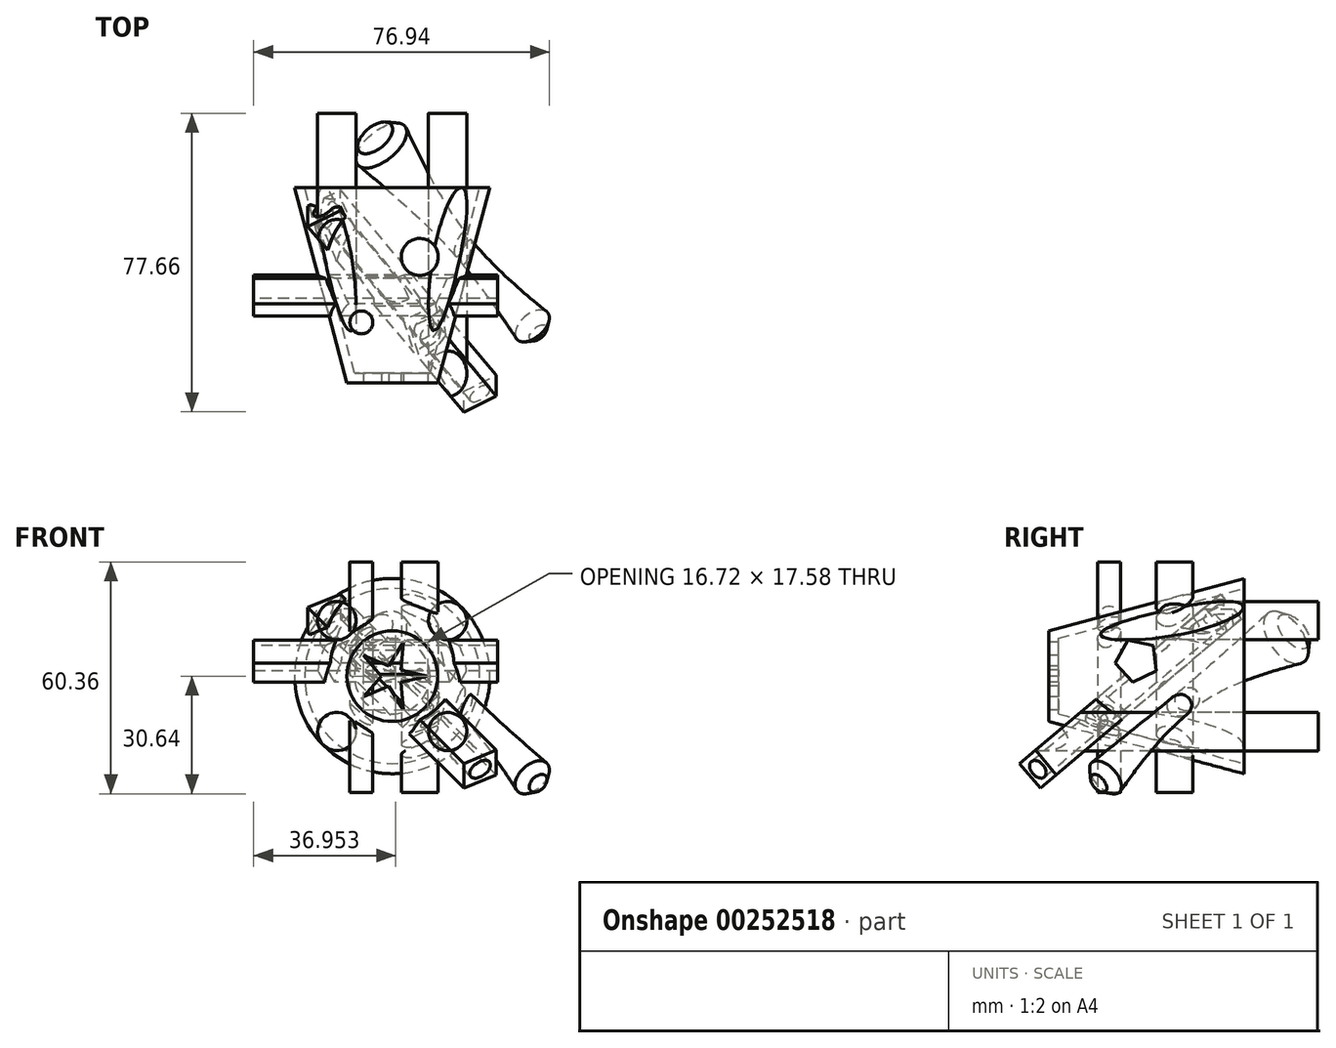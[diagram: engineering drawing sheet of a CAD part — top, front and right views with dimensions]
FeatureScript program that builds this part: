
annotation { "Feature Type Name" : "Feature", "Feature Type Description" : "" }
export const myFeature = defineFeature(function(context is Context, id is Id, definition is map)
    precondition{}
    {
        {
            var Q0;
            Q0=qCreatedBy(makeId("Front.planeOp"),FACE);
            var sketch = newSketch(context, id + "F0", { "sketchPlane" : qUnion([Q0])});
            skCircle(sketch, "E0", {"center": v(0, 0) * mm, "radius": 25.4 * mm});
            skSolve(sketch);
        }
        {
            var Q0;
            Q0 = qSketchRegion(id + "F0", true);
            extrude(context, id + "F1", {"entities" : qUnion([Q0]), "depth" : 50.8 * mm, "offsetDistance" : 25.4 * mm, "hasDraft" : true, "draftAngle" : 15 * degree, "draftPullDirection" : true});
        }
        {
            var Q0;
            Q0=makeQuery(id+"F1.opExtrude","CAP_FACE",FACE,{"disambiguationData":[OSD([sQuery(id+"F0.wireOp",EDGE,"E0")])],"isStart":true});
            shell(context, id + "F2", {"entities" : qUnion([Q0]), "thickness" : 2.54 * mm});
        }
        {
            var Q0;
            Q0=qCreatedBy(makeId("Top.planeOp"),FACE);
            cPlane(context, id + "F3", {"entities" : qUnion([Q0]), "cplaneType" : CPlaneType.OFFSET, "offset" : 30.23 * mm, "oppositeDirection" : true, "width" : 152.4 * mm, "height" : 152.4 * mm});
        }
        {
            var Q0;
            Q0=qCreatedBy(id+"F3.planeOp",FACE);
            var sketch = newSketch(context, id + "F4", { "sketchPlane" : qUnion([Q0])});
            skCircle(sketch, "E1", {"center": v(-8.03, -35.07) * mm, "radius": 2.99 * mm});
            skCircle(sketch, "E2", {"center": v(7.15, -18.05) * mm, "radius": 4.8 * mm});
            skSolve(sketch);
        }
        {
            var Q0;
            Q0 = qSketchRegion(id + "F4", true);
            extrude(context, id + "F5", {"entities" : qUnion([Q0]), "operationType" : NewBodyOperationType.ADD, "depth" : 59.94 * mm, "offsetDistance" : 25.4 * mm});
        }
        {
            var Q0;
            Q0=qCreatedBy(makeId("Right.planeOp"),FACE);
            cPlane(context, id + "F6", {"entities" : qUnion([Q0]), "cplaneType" : CPlaneType.OFFSET, "offset" : 36.07 * mm, "oppositeDirection" : true, "width" : 152.4 * mm, "height" : 152.4 * mm});
        }
        {
            var Q0;
            Q0=qCreatedBy(id+"F6.planeOp",FACE);
            var sketch = newSketch(context, id + "F7", { "sketchPlane" : qUnion([Q0])});
            skCircle(sketch, "E3.cCircle", {"center": v(-27.79, 4.1) * mm, "radius": 5.72 * mm, "construction": true});
            skLineSegment(sketch, "E3.0", {"start": v(-22.78, 1.33) * mm, "end": v(-28.88, -1.51) * mm});
            skLineSegment(sketch, "E3.1", {"start": v(-28.88, -1.51) * mm, "end": v(-33.47, 3.4) * mm});
            skLineSegment(sketch, "E3.2", {"start": v(-33.47, 3.4) * mm, "end": v(-30.21, 9.29) * mm});
            skLineSegment(sketch, "E3.3", {"start": v(-30.21, 9.29) * mm, "end": v(-23.6, 8) * mm});
            skLineSegment(sketch, "E3.4", {"start": v(-23.6, 8) * mm, "end": v(-22.78, 1.33) * mm});
            skSolve(sketch);
        }
        {
            var Q0;
            Q0 = qSketchRegion(id + "F7", true);
            extrude(context, id + "F8", {"entities" : qUnion([Q0]), "operationType" : NewBodyOperationType.ADD, "depth" : 63.5 * mm, "offsetDistance" : 25.4 * mm});
        }
        {
            var Q0;
            Q0=makeQuery(id+"F1.opExtrude","CAP_FACE",FACE,{"disambiguationData":[OSD([sQuery(id+"F0.wireOp",EDGE,"E0")])],"isStart":false});
            var sketch = newSketch(context, id + "F9", { "sketchPlane" : qUnion([Q0])});
            skLineSegment(sketch, "E4", {"start": v(0, 0) * mm, "end": v(9.24, 0) * mm});
            skCircle(sketch, "E5.cCircle", {"center": v(0, 0) * mm, "radius": 9.24 * mm, "construction": true});
            skLineSegment(sketch, "E5.0", {"start": v(9.24, 0) * mm, "end": v(2.86, -8.8) * mm});
            skLineSegment(sketch, "E5.1", {"start": v(2.86, -8.8) * mm, "end": v(-7.48, -5.43) * mm});
            skLineSegment(sketch, "E5.2", {"start": v(-7.48, -5.43) * mm, "end": v(-7.48, 5.43) * mm});
            skLineSegment(sketch, "E5.3", {"start": v(-7.48, 5.43) * mm, "end": v(2.86, 8.8) * mm});
            skLineSegment(sketch, "E5.4", {"start": v(2.86, 8.8) * mm, "end": v(9.24, 0) * mm});
            skLineSegment(sketch, "E6", {"start": v(0, 0) * mm, "end": v(2.86, -8.8) * mm});
            skLineSegment(sketch, "E7", {"start": v(0, 0) * mm, "end": v(-7.48, -5.43) * mm});
            skLineSegment(sketch, "E8", {"start": v(0, 0) * mm, "end": v(-7.48, 5.43) * mm});
            skLineSegment(sketch, "E9", {"start": v(0, 0) * mm, "end": v(2.86, 8.8) * mm});
            skCircle(sketch, "E10.cCircle", {"center": v(0, 0) * mm, "radius": 2.25 * mm, "construction": true});
            skLineSegment(sketch, "E10.0", {"start": v(2.25, 1.63) * mm, "end": v(2.25, -1.63) * mm});
            skLineSegment(sketch, "E10.1", {"start": v(2.25, -1.63) * mm, "end": v(-0.86, -2.64) * mm});
            skLineSegment(sketch, "E10.2", {"start": v(-0.86, -2.64) * mm, "end": v(-2.78, 0) * mm});
            skLineSegment(sketch, "E10.3", {"start": v(-2.78, 0) * mm, "end": v(-0.86, 2.64) * mm});
            skLineSegment(sketch, "E10.4", {"start": v(-0.86, 2.64) * mm, "end": v(2.25, 1.63) * mm});
            skPoint(sketch, "E10.0.midPoint", {"position": v(2.25, 0) * mm});
            skLineSegment(sketch, "E11", {"start": v(2.25, -1.63) * mm, "end": v(2.86, -8.8) * mm});
            skLineSegment(sketch, "E12", {"start": v(2.86, -8.8) * mm, "end": v(-0.86, -2.64) * mm});
            skLineSegment(sketch, "E13", {"start": v(-0.86, -2.64) * mm, "end": v(-7.48, -5.43) * mm});
            skLineSegment(sketch, "E14", {"start": v(-7.48, -5.43) * mm, "end": v(-2.78, 0) * mm});
            skLineSegment(sketch, "E15", {"start": v(-2.78, 0) * mm, "end": v(-7.48, 5.43) * mm});
            skLineSegment(sketch, "E16", {"start": v(-0.86, 2.64) * mm, "end": v(-7.48, 5.43) * mm});
            skLineSegment(sketch, "E17", {"start": v(-0.86, 2.64) * mm, "end": v(2.86, 8.8) * mm});
            skLineSegment(sketch, "E18", {"start": v(2.25, 1.63) * mm, "end": v(2.86, 8.8) * mm});
            skLineSegment(sketch, "E19", {"start": v(2.25, 1.63) * mm, "end": v(9.24, 0) * mm});
            skLineSegment(sketch, "E20", {"start": v(2.25, -1.63) * mm, "end": v(9.24, 0) * mm});
            skSolve(sketch);
        }
        {
            var Q0;
            {var subQ0=sQuery(id+"F9.wireOp",EDGE,"E19");Q0=makeQuery(id+"F9.imprint","IMPRINT",FACE,{"disambiguationData":[TD([[makeQuery(id+"F9.imprint","IMPRINT",EDGE,{"derivedFrom":subQ0}),-1.0]])]});}
            var Q1;
            {var subQ0=sQuery(id+"F9.wireOp",EDGE,"E20");Q1=makeQuery(id+"F9.imprint","IMPRINT",FACE,{"disambiguationData":[TD([[makeQuery(id+"F9.imprint","IMPRINT",EDGE,{"derivedFrom":subQ0}),1.0]])]});}
            var Q2;
            {var subQ0=sQuery(id+"F9.wireOp",EDGE,"E11");Q2=makeQuery(id+"F9.imprint","IMPRINT",FACE,{"disambiguationData":[TD([[makeQuery(id+"F9.imprint","IMPRINT",EDGE,{"derivedFrom":subQ0}),-1.0]])]});}
            var Q3;
            {var subQ0=sQuery(id+"F9.wireOp",EDGE,"E12");Q3=makeQuery(id+"F9.imprint","IMPRINT",FACE,{"disambiguationData":[TD([[makeQuery(id+"F9.imprint","IMPRINT",EDGE,{"derivedFrom":subQ0}),-1.0]])]});}
            var Q4;
            {var subQ0=sQuery(id+"F9.wireOp",EDGE,"E13");Q4=makeQuery(id+"F9.imprint","IMPRINT",FACE,{"disambiguationData":[TD([[makeQuery(id+"F9.imprint","IMPRINT",EDGE,{"derivedFrom":subQ0}),-1.0]])]});}
            var Q5;
            {var subQ0=sQuery(id+"F9.wireOp",EDGE,"E14");Q5=makeQuery(id+"F9.imprint","IMPRINT",FACE,{"disambiguationData":[TD([[makeQuery(id+"F9.imprint","IMPRINT",EDGE,{"derivedFrom":subQ0}),-1.0]])]});}
            var Q6;
            {var subQ0=sQuery(id+"F9.wireOp",EDGE,"E15");Q6=makeQuery(id+"F9.imprint","IMPRINT",FACE,{"disambiguationData":[TD([[makeQuery(id+"F9.imprint","IMPRINT",EDGE,{"derivedFrom":subQ0}),-1.0]])]});}
            var Q7;
            {var subQ0=sQuery(id+"F9.wireOp",EDGE,"E16");Q7=makeQuery(id+"F9.imprint","IMPRINT",FACE,{"disambiguationData":[TD([[makeQuery(id+"F9.imprint","IMPRINT",EDGE,{"derivedFrom":subQ0}),1.0]])]});}
            var Q8;
            {var subQ0=sQuery(id+"F9.wireOp",EDGE,"E17");Q8=makeQuery(id+"F9.imprint","IMPRINT",FACE,{"disambiguationData":[TD([[makeQuery(id+"F9.imprint","IMPRINT",EDGE,{"derivedFrom":subQ0}),-1.0]])]});}
            var Q9;
            {var subQ0=sQuery(id+"F9.wireOp",EDGE,"E18");Q9=makeQuery(id+"F9.imprint","IMPRINT",FACE,{"disambiguationData":[TD([[makeQuery(id+"F9.imprint","IMPRINT",EDGE,{"derivedFrom":subQ0}),1.0]])]});}
            var Q10;
            {var subQ1=sQuery(id+"F9.wireOp",EDGE,"E4");var subQ3=sQuery(id+"F9.wireOp",EDGE,"E10.0");var subQ4=makeQuery(id+"F9.imprint","INTERSECT",VERTEX,{"derivedFrom":[subQ1,subQ3]});Q10=makeQuery(id+"F9.imprint","IMPRINT",FACE,{"disambiguationData":[TD([[makeQuery(id+"F9.imprint","IMPRINT",EDGE,{"disambiguationData":[TD([[subQ4,1.0]])],"derivedFrom":subQ3}),-1.0]])]});}
            var Q11;
            {var subQ1=sQuery(id+"F9.wireOp",EDGE,"E4");var subQ3=sQuery(id+"F9.wireOp",EDGE,"E10.0");var subQ4=makeQuery(id+"F9.imprint","INTERSECT",VERTEX,{"derivedFrom":[subQ1,subQ3]});Q11=makeQuery(id+"F9.imprint","IMPRINT",FACE,{"disambiguationData":[TD([[makeQuery(id+"F9.imprint","IMPRINT",EDGE,{"disambiguationData":[TD([[subQ4,-1.0]])],"derivedFrom":subQ3}),-1.0]])]});}
            var Q12;
            {var subQ1=sQuery(id+"F9.wireOp",EDGE,"E6");var subQ3=sQuery(id+"F9.wireOp",EDGE,"E10.1");var subQ4=makeQuery(id+"F9.imprint","INTERSECT",VERTEX,{"derivedFrom":[subQ1,subQ3]});Q12=makeQuery(id+"F9.imprint","IMPRINT",FACE,{"disambiguationData":[TD([[makeQuery(id+"F9.imprint","IMPRINT",EDGE,{"disambiguationData":[TD([[subQ4,-1.0]])],"derivedFrom":subQ3}),-1.0]])]});}
            var Q13;
            {var subQ1=sQuery(id+"F9.wireOp",EDGE,"E7");var subQ3=sQuery(id+"F9.wireOp",EDGE,"E10.2");var subQ4=makeQuery(id+"F9.imprint","INTERSECT",VERTEX,{"derivedFrom":[subQ1,subQ3]});Q13=makeQuery(id+"F9.imprint","IMPRINT",FACE,{"disambiguationData":[TD([[makeQuery(id+"F9.imprint","IMPRINT",EDGE,{"disambiguationData":[TD([[subQ4,-1.0]])],"derivedFrom":subQ3}),-1.0]])]});}
            var Q14;
            {var subQ1=sQuery(id+"F9.wireOp",EDGE,"E8");var subQ3=sQuery(id+"F9.wireOp",EDGE,"E10.3");var subQ4=makeQuery(id+"F9.imprint","INTERSECT",VERTEX,{"derivedFrom":[subQ1,subQ3]});Q14=makeQuery(id+"F9.imprint","IMPRINT",FACE,{"disambiguationData":[TD([[makeQuery(id+"F9.imprint","IMPRINT",EDGE,{"disambiguationData":[TD([[subQ4,-1.0]])],"derivedFrom":subQ3}),-1.0]])]});}
            extrude(context, id + "F10", {"entities" : qUnion([Q0, Q1, Q2, Q3, Q4, Q5, Q6, Q7, Q8, Q9, Q10, Q11, Q12, Q13, Q14]), "operationType" : NewBodyOperationType.REMOVE, "oppositeDirection" : true, "depth" : 6.12 * mm, "offsetDistance" : 25.4 * mm});
        }
        {
            var Q0;
            Q0=qCreatedBy(makeId("Right.planeOp"),FACE);
            var Q1;
            Q1=qCreatedBy(makeId("Top.planeOp"),FACE);
            cPlane(context, id + "F11", {"entities" : qUnion([Q0, Q1]), "cplaneType" : CPlaneType.MID_PLANE, "offset" : 25.4 * mm, "width" : 152.4 * mm, "height" : 152.4 * mm});
        }
        {
            var Q0;
            Q0=qCreatedBy(id+"F11.planeOp",FACE);
            var sketch = newSketch(context, id + "F12", { "sketchPlane" : qUnion([Q0])});
            skLineSegment(sketch, "E21", {"start": v(-57.7, -39.88) * mm, "end": v(-57.7, 43.62) * mm});
            skSolve(sketch);
        }
        {
            var Q0;
            Q0=sQuery(id+"F12.wireOp",EDGE,"E21");
            cPlane(context, id + "F13", {"entities" : qUnion([Q0]), "cplaneType" : CPlaneType.LINE_ANGLE, "offset" : 25.4 * mm, "angle" : 50 * degree, "width" : 152.4 * mm, "height" : 152.4 * mm});
        }
        {
            var Q0;
            Q0=qCreatedBy(id+"F13.planeOp",FACE);
            cPlane(context, id + "F14", {"entities" : qUnion([Q0]), "cplaneType" : CPlaneType.OFFSET, "offset" : 22.86 * mm, "oppositeDirection" : true, "width" : 152.4 * mm, "height" : 152.4 * mm});
        }
        {
            var Q0;
            Q0=qCreatedBy(id+"F14.planeOp",FACE);
            var sketch = newSketch(context, id + "F15", { "sketchPlane" : qUnion([Q0])});
            skLineSegment(sketch, "E22.bottom", {"start": v(16.48, 20.18) * mm, "end": v(6.41, 20.18) * mm});
            skLineSegment(sketch, "E22.top", {"start": v(16.48, 11.81) * mm, "end": v(6.41, 11.81) * mm});
            skLineSegment(sketch, "E22.left", {"start": v(16.48, 20.18) * mm, "end": v(16.48, 11.81) * mm});
            skLineSegment(sketch, "E22.right", {"start": v(6.41, 20.18) * mm, "end": v(6.41, 11.81) * mm});
            skEllipse(sketch, "E23", {"center": v(11.44, 16) * mm, "majorRadius": 3.22 * mm, "minorRadius": 2.64 * mm, "majorAxis": v(1, 0)});
            skPoint(sketch, "E23.centerSnap0", {"position": v(16.48, 16) * mm});
            skPoint(sketch, "E23.centerSnap1", {"position": v(11.44, 20.18) * mm});
            skCircle(sketch, "E24", {"center": v(-6.48, 2.76) * mm, "radius": 5.62 * mm});
            skSolve(sketch);
        }
        {
            var Q0;
            Q0=makeQuery(id+"F15.imprint","IMPRINT",FACE,{"disambiguationData":[TD([[makeQuery(id+"F15.imprint","IMPRINT",EDGE,{"derivedFrom":sQuery(id+"F15.wireOp",EDGE,"E22.bottom")}),1.0]])]});
            extrude(context, id + "F16", {"entities" : qUnion([Q0]), "operationType" : NewBodyOperationType.ADD, "depth" : 74.93 * mm, "offsetDistance" : 25.4 * mm});
        }
        {
            var Q0;
            Q0=qCreatedBy(id+"F13.planeOp",FACE);
            cPlane(context, id + "F17", {"entities" : qUnion([Q0]), "cplaneType" : CPlaneType.OFFSET, "offset" : 19.8 * mm, "width" : 152.4 * mm, "height" : 152.4 * mm});
        }
        {
            var Q0;
            Q0=qCreatedBy(id+"F13.planeOp",FACE);
            cPlane(context, id + "F18", {"entities" : qUnion([Q0]), "cplaneType" : CPlaneType.OFFSET, "offset" : 54.1 * mm, "width" : 152.4 * mm, "height" : 152.4 * mm});
        }
        {
            var Q0;
            Q0=qCreatedBy(id+"F17.planeOp",FACE);
            var sketch = newSketch(context, id + "F19", { "sketchPlane" : qUnion([Q0])});
            skCircle(sketch, "E25", {"center": v(-6.56, 4.63) * mm, "radius": 3.14 * mm});
            skSolve(sketch);
        }
        {
            var Q0;
            Q0=qCreatedBy(id+"F18.planeOp",FACE);
            var sketch = newSketch(context, id + "F20", { "sketchPlane" : qUnion([Q0])});
            skCircle(sketch, "E26", {"center": v(-5.54, 0) * mm, "radius": 8.55 * mm});
            skSolve(sketch);
        }
        {
            var Q1;
            Q1=makeQuery(id+"F15.imprint","IMPRINT",FACE,{"disambiguationData":[TD([[makeQuery(id+"F15.imprint","IMPRINT",EDGE,{"derivedFrom":sQuery(id+"F15.wireOp",EDGE,"E24")}),1.0]])]});
            var Q2;
            Q2=makeQuery(id+"F19.imprint","IMPRINT",FACE,{"disambiguationData":[TD([[makeQuery(id+"F19.imprint","IMPRINT",EDGE,{"derivedFrom":sQuery(id+"F19.wireOp",EDGE,"E25")}),1.0]])]});
            var Q3;
            Q3=makeQuery(id+"F20.imprint","IMPRINT",FACE,{"disambiguationData":[TD([[makeQuery(id+"F20.imprint","IMPRINT",EDGE,{"derivedFrom":sQuery(id+"F20.wireOp",EDGE,"E26")}),1.0]])]});
            loft(context, id + "F21", {"operationType" : NewBodyOperationType.ADD, "sheetProfilesArray" : [{ "sheetProfileEntities" : qUnion([Q1]) }, { "sheetProfileEntities" : qUnion([Q2]) }, { "sheetProfileEntities" : qUnion([Q3]) }]});
        }
        {
            var Q0;
            Q0=makeQuery(id+"F21.opLoft","MID_CAP_EDGE",EDGE,{"disambiguationData":[OSD([sQuery(id+"F15.wireOp",EDGE,"E24")])],"capPos":0.0});
            var Q1;
            Q1=makeQuery(id+"F21.opLoft","MID_CAP_EDGE",EDGE,{"disambiguationData":[OSD([sQuery(id+"F20.wireOp",EDGE,"E26")])],"capPos":2.0});
            chamfer(context, id + "F22", {"entities" : qUnion([Q0, Q1]), "width" : 2.54 * mm, "tangentPropagation" : true});
        }
        {
            var Q0;
            Q0=makeQuery(id+"F1.opExtrude","CAP_FACE",FACE,{"disambiguationData":[OSD([sQuery(id+"F0.wireOp",EDGE,"E0")])],"isStart":true});
            var sketch = newSketch(context, id + "F23", { "sketchPlane" : qUnion([Q0])});
            skCircle(sketch, "E27", {"center": v(0, 0) * mm, "radius": 25.4 * mm});
            skCircle(sketch, "E28", {"center": v(0, 0) * mm, "radius": 22.77 * mm});
            skLineSegment(sketch, "E29.0", {"start": v(28.2, -28.2) * mm, "end": v(-30.85, 30.85) * mm});
            skCircle(sketch, "E30", {"center": v(-14.42, 14.42) * mm, "radius": 5 * mm});
            skCircle(sketch, "E31.1.0", {"center": v(-14.42, -14.42) * mm, "radius": 5 * mm});
            skCircle(sketch, "E31.2.0", {"center": v(14.42, -14.42) * mm, "radius": 5 * mm});
            skCircle(sketch, "E31.3.0", {"center": v(14.42, 14.42) * mm, "radius": 5 * mm});
            skSolve(sketch);
        }
        {
            var Q0;
            {var subQ0=sQuery(id+"F23.wireOp",EDGE,"E30");var subQ1=sQuery(id+"F23.wireOp",EDGE,"E28");var subQ2=makeQuery(id+"F23.imprint","INTERSECT",VERTEX,{"disambiguationData":[OD(0.0)],"derivedFrom":[subQ1,subQ0]});Q0=makeQuery(id+"F23.imprint","IMPRINT",FACE,{"disambiguationData":[TD([[makeQuery(id+"F23.imprint","IMPRINT",EDGE,{"disambiguationData":[TD([[subQ2,-1.0]])],"derivedFrom":subQ1}),-1.0]])]});}
            var Q1;
            {var subQ0=sQuery(id+"F23.wireOp",EDGE,"E29.0");var subQ1=sQuery(id+"F23.wireOp",EDGE,"E28");var subQ2=makeQuery(id+"F23.imprint","INTERSECT",VERTEX,{"disambiguationData":[OD(0.0)],"derivedFrom":[subQ1,subQ0]});Q1=makeQuery(id+"F23.imprint","IMPRINT",FACE,{"disambiguationData":[TD([[makeQuery(id+"F23.imprint","IMPRINT",EDGE,{"disambiguationData":[TD([[subQ2,-1.0]])],"derivedFrom":subQ1}),-1.0]])]});}
            var Q2;
            {var subQ0=sQuery(id+"F23.wireOp",EDGE,"E29.0");var subQ1=sQuery(id+"F23.wireOp",EDGE,"E28");var subQ2=makeQuery(id+"F23.imprint","INTERSECT",VERTEX,{"disambiguationData":[OD(0.0)],"derivedFrom":[subQ1,subQ0]});Q2=makeQuery(id+"F23.imprint","IMPRINT",FACE,{"disambiguationData":[TD([[makeQuery(id+"F23.imprint","IMPRINT",EDGE,{"disambiguationData":[TD([[subQ2,-1.0]])],"derivedFrom":subQ1}),1.0]])]});}
            var Q3;
            {var subQ0=sQuery(id+"F23.wireOp",EDGE,"E30");var subQ1=sQuery(id+"F23.wireOp",EDGE,"E28");var subQ2=makeQuery(id+"F23.imprint","INTERSECT",VERTEX,{"disambiguationData":[OD(0.0)],"derivedFrom":[subQ1,subQ0]});Q3=makeQuery(id+"F23.imprint","IMPRINT",FACE,{"disambiguationData":[TD([[makeQuery(id+"F23.imprint","IMPRINT",EDGE,{"disambiguationData":[TD([[subQ2,-1.0]])],"derivedFrom":subQ1}),1.0]])]});}
            var Q4;
            {var subQ0=sQuery(id+"F23.wireOp",EDGE,"E31.3.0");var subQ1=sQuery(id+"F23.wireOp",EDGE,"E28");var subQ2=makeQuery(id+"F23.imprint","INTERSECT",VERTEX,{"disambiguationData":[OD(0.0)],"derivedFrom":[subQ1,subQ0]});Q4=makeQuery(id+"F23.imprint","IMPRINT",FACE,{"disambiguationData":[TD([[makeQuery(id+"F23.imprint","IMPRINT",EDGE,{"disambiguationData":[TD([[subQ2,-1.0]])],"derivedFrom":subQ1}),-1.0]])]});}
            var Q5;
            {var subQ0=sQuery(id+"F23.wireOp",EDGE,"E31.3.0");var subQ1=sQuery(id+"F23.wireOp",EDGE,"E28");var subQ2=makeQuery(id+"F23.imprint","INTERSECT",VERTEX,{"disambiguationData":[OD(0.0)],"derivedFrom":[subQ1,subQ0]});Q5=makeQuery(id+"F23.imprint","IMPRINT",FACE,{"disambiguationData":[TD([[makeQuery(id+"F23.imprint","IMPRINT",EDGE,{"disambiguationData":[TD([[subQ2,-1.0]])],"derivedFrom":subQ1}),1.0]])]});}
            var Q6;
            {var subQ0=sQuery(id+"F23.wireOp",EDGE,"E31.1.0");var subQ1=sQuery(id+"F23.wireOp",EDGE,"E28");var subQ2=makeQuery(id+"F23.imprint","INTERSECT",VERTEX,{"disambiguationData":[OD(0.0)],"derivedFrom":[subQ1,subQ0]});Q6=makeQuery(id+"F23.imprint","IMPRINT",FACE,{"disambiguationData":[TD([[makeQuery(id+"F23.imprint","IMPRINT",EDGE,{"disambiguationData":[TD([[subQ2,1.0]])],"derivedFrom":subQ1}),-1.0]])]});}
            var Q7;
            {var subQ0=sQuery(id+"F23.wireOp",EDGE,"E31.1.0");var subQ1=sQuery(id+"F23.wireOp",EDGE,"E28");var subQ2=makeQuery(id+"F23.imprint","INTERSECT",VERTEX,{"disambiguationData":[OD(0.0)],"derivedFrom":[subQ1,subQ0]});Q7=makeQuery(id+"F23.imprint","IMPRINT",FACE,{"disambiguationData":[TD([[makeQuery(id+"F23.imprint","IMPRINT",EDGE,{"disambiguationData":[TD([[subQ2,1.0]])],"derivedFrom":subQ1}),1.0]])]});}
            var Q8;
            {var subQ0=sQuery(id+"F23.wireOp",EDGE,"E29.0");var subQ1=sQuery(id+"F23.wireOp",EDGE,"E28");var subQ2=makeQuery(id+"F23.imprint","INTERSECT",VERTEX,{"disambiguationData":[OD(1.0)],"derivedFrom":[subQ1,subQ0]});Q8=makeQuery(id+"F23.imprint","IMPRINT",FACE,{"disambiguationData":[TD([[makeQuery(id+"F23.imprint","IMPRINT",EDGE,{"disambiguationData":[TD([[subQ2,-1.0]])],"derivedFrom":subQ1}),-1.0]])]});}
            var Q9;
            {var subQ0=sQuery(id+"F23.wireOp",EDGE,"E31.2.0");var subQ1=sQuery(id+"F23.wireOp",EDGE,"E28");var subQ2=makeQuery(id+"F23.imprint","INTERSECT",VERTEX,{"disambiguationData":[OD(0.0)],"derivedFrom":[subQ1,subQ0]});Q9=makeQuery(id+"F23.imprint","IMPRINT",FACE,{"disambiguationData":[TD([[makeQuery(id+"F23.imprint","IMPRINT",EDGE,{"disambiguationData":[TD([[subQ2,-1.0]])],"derivedFrom":subQ1}),-1.0]])]});}
            var Q10;
            {var subQ0=sQuery(id+"F23.wireOp",EDGE,"E31.2.0");var subQ1=sQuery(id+"F23.wireOp",EDGE,"E28");var subQ2=makeQuery(id+"F23.imprint","INTERSECT",VERTEX,{"disambiguationData":[OD(0.0)],"derivedFrom":[subQ1,subQ0]});Q10=makeQuery(id+"F23.imprint","IMPRINT",FACE,{"disambiguationData":[TD([[makeQuery(id+"F23.imprint","IMPRINT",EDGE,{"disambiguationData":[TD([[subQ2,-1.0]])],"derivedFrom":subQ1}),1.0]])]});}
            var Q11;
            {var subQ0=sQuery(id+"F23.wireOp",EDGE,"E29.0");var subQ1=sQuery(id+"F23.wireOp",EDGE,"E28");var subQ2=makeQuery(id+"F23.imprint","INTERSECT",VERTEX,{"disambiguationData":[OD(1.0)],"derivedFrom":[subQ1,subQ0]});Q11=makeQuery(id+"F23.imprint","IMPRINT",FACE,{"disambiguationData":[TD([[makeQuery(id+"F23.imprint","IMPRINT",EDGE,{"disambiguationData":[TD([[subQ2,-1.0]])],"derivedFrom":subQ1}),1.0]])]});}
            var Q12;
            Q12=makeQuery(id+"F1.opExtrude","SWEPT_BODY",BODY,{"disambiguationData":[OSD([sQuery(id+"F0.wireOp",EDGE,"E0")])]});
            extrude(context, id + "F24", {"entities" : qUnion([Q0, Q1, Q2, Q3, Q4, Q5, Q6, Q7, Q8, Q9, Q10, Q11]), "depth" : 19.3 * mm, "offsetDistance" : 25.4 * mm, "hasSecondDirection" : true, "secondDirectionBound" : SecondDirectionBoundingType.UP_TO_BODY, "secondDirectionOppositeDirection" : true, "secondDirectionDepth" : 25.4 * mm, "secondDirectionBoundEntityBody" : qUnion([Q12])});
        }
    });
